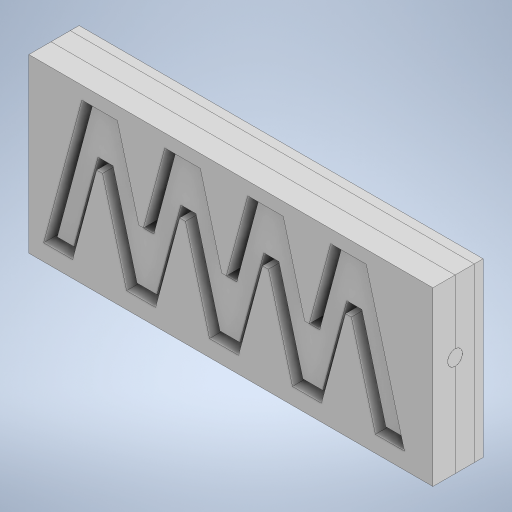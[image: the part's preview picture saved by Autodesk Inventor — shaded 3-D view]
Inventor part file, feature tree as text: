
AUTODESK INVENTOR PART (.ipt)
format: ipt  version: 2024 (Build 280153000, 153)  size: 589,312 bytes
history: native  units: mm
features: extrude x9, sketch x8, plane x4, split x4, boolean_combine x2, projected_geometry x2, other x2, pattern_linear x1, chamfer x1, shell x1
ambient origin geometry x8: Origin, YZ Plane, XZ Plane, XY Plane, X Axis, Y Axis, Z Axis, Center Point
bodies: Solid1 (feature_tree), Solid2 (feature_tree), Solid3 (feature_tree), Solid4 (feature_tree), Solid5 (feature_tree), Solid6 (feature_tree), Solid7 (feature_tree), Solid8 (feature_tree), Solid9 (feature_tree), Solid10 (feature_tree)
feature tree (34):
  extrude  "Extrusion1"  TaperAngle=75.0deg  [1 undecoded]
  pattern_linear  "Rectangular Pattern1"  Count1=5  [1 undecoded]
  chamfer  "Chamfer1"  Distance=15.0mm
  shell  "Shell1"  Thickness=40.0mm
  sketch  "Sketch2"  dims[d3=18.0mm]
  extrude  "Extrusion2"  Depth=2.0mm
  extrude  "Extrusion3"  Depth=2.0mm
  extrude  "Extrusion4"  Depth=3.0mm TaperAngle=0.0deg
  extrude  "Extrusion5"  Depth=10.0mm TaperAngle=0.0deg
  boolean_combine  "Combine1"
  extrude  "Extrusion6"  Depth=3.0mm TaperAngle=0.0deg
  plane  "Work Plane1"
  split  "Split1"
  split  "Split2"
  boolean_combine  "Combine2"
  plane  "Work Plane2"
  sketch  "Sketch9"  dims[d17=4.0mm d18=0.0mm d19=3.0mm d20=0.0mm]
  sketch  "Sketch10"  dims[d21=1.0mm d22=0.0mm d23=0.5mm d24=0.0mm d25=3.0mm d26=0.0mm d27=0.0mm d28=31.0mm d29=0.0mm d30=3.0mm d31=2.0mm d32=45.0deg d33=0.0mm d34=0.0mm d35=0.0mm d39=62.5mm d40=0.0mm d41=10.0mm d42=0.0mm]
  extrude  "Extrusion7"  TaperAngle=0.0deg  [1 undecoded]
  split  "Split3"
  plane  "Work Plane3"
  split  "Split4"
  plane  "Work Plane4"
  extrude  "Extrusion8"  Depth=10.0mm TaperAngle=0.0deg
  sketch  "Sketch1"  dims[d0=75.0deg d1=75.0deg d2=50.0mm]
  sketch  "Sketch3"  dims[d4=2.0mm]
  sketch  "Sketch4"  dims[d5=12.0mm d6=15.0mm d7=0.0mm d8=40.0mm d10=28.058819mm]
  sketch  "Sketch5"  dims[d12=28.058819mm d13=2.0mm]
  projected_geometry  "Projected Loop1"
  sketch  "Sketch7"  dims[d14=5.0mm d16=2.0mm]
  other  "Srf1"
  other  "Work Axis1"
  projected_geometry  "Projected Loop3"
  extrude  "ExtrusionSrf1"  Depth=3.0mm TaperAngle=45.0deg
note: 3 required parameter values undecoded (feature->parameter linkage not recoverable at this tier; creation-order binding heuristic only, values carry confidence <= 0.55)
